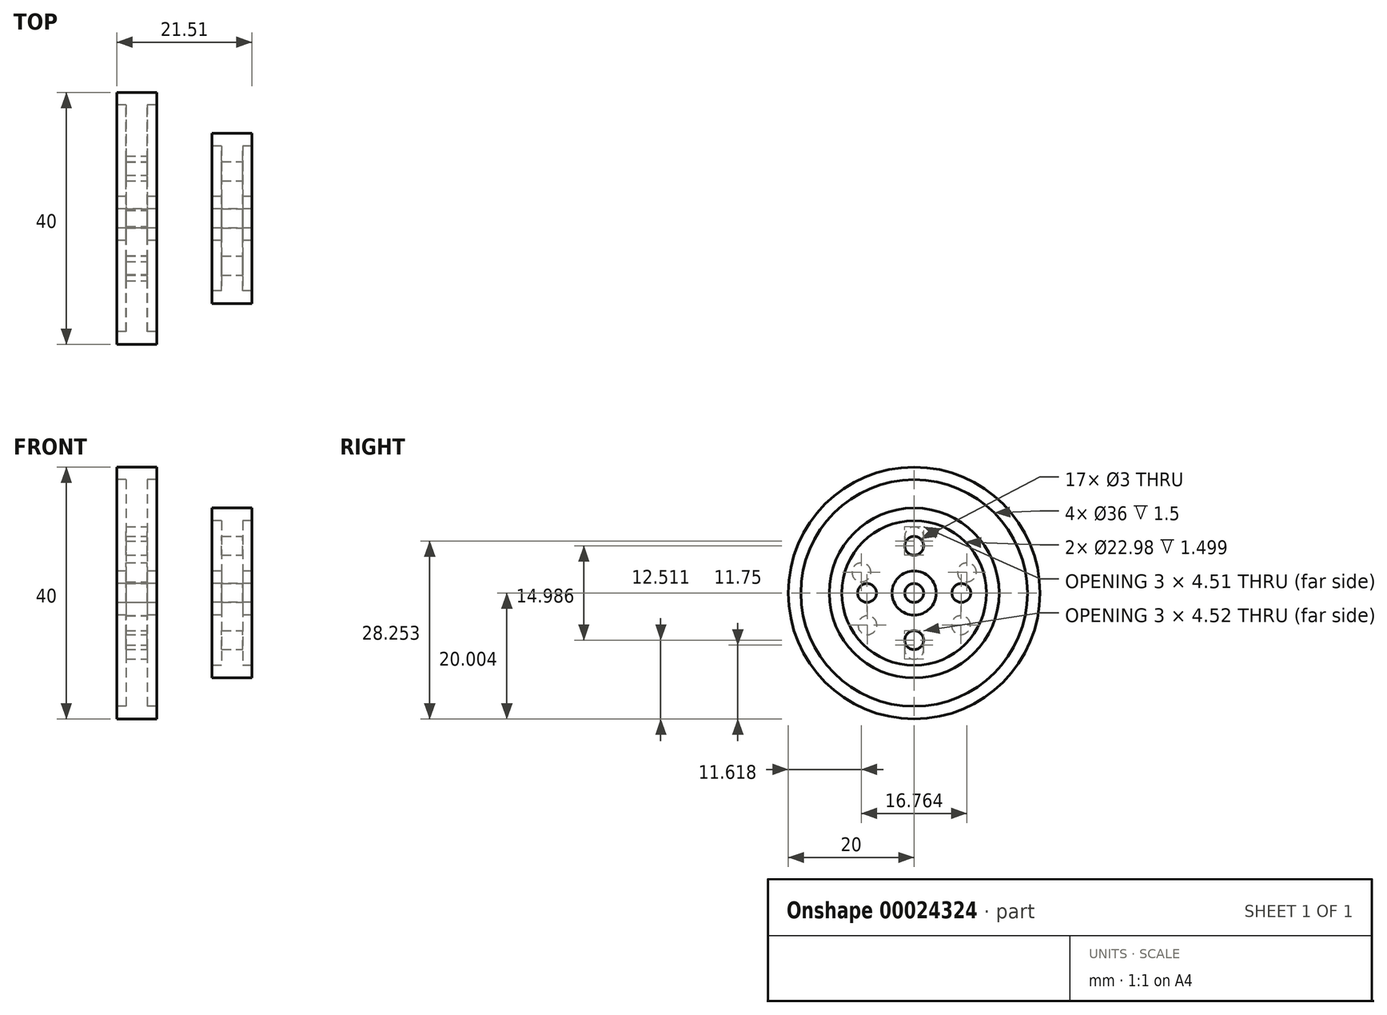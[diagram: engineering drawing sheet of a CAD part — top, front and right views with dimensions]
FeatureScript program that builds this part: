
annotation { "Feature Type Name" : "Feature", "Feature Type Description" : "" }
export const myFeature = defineFeature(function(context is Context, id is Id, definition is map)
    precondition{}
    {
        {
            var Q0;
            Q0=qCreatedBy(makeId("Front.planeOp"),FACE);
            var sketch = newSketch(context, id + "F0", { "sketchPlane" : qUnion([Q0])});
            skLineSegment(sketch, "E0.bottom", {"start": v(-7.32, 15.41) * mm, "end": v(-3.97, 15.41) * mm});
            skLineSegment(sketch, "E0.top", {"start": v(-7.32, -3.09) * mm, "end": v(-3.97, -3.09) * mm});
            skLineSegment(sketch, "E0.left", {"start": v(-7.32, 15.41) * mm, "end": v(-7.32, -3.09) * mm});
            skLineSegment(sketch, "E0.right", {"start": v(-3.97, 15.41) * mm, "end": v(-3.97, -3.09) * mm});
            skLineSegment(sketch, "E1.bottom", {"start": v(-8.82, -3.09) * mm, "end": v(-2.47, -3.09) * mm});
            skLineSegment(sketch, "E1.top", {"start": v(-8.82, -1.09) * mm, "end": v(-2.47, -1.09) * mm});
            skLineSegment(sketch, "E1.left", {"start": v(-8.82, -3.09) * mm, "end": v(-8.82, -1.09) * mm});
            skLineSegment(sketch, "E1.right", {"start": v(-2.47, -3.09) * mm, "end": v(-2.47, -1.09) * mm});
            skLineSegment(sketch, "E2.bottom", {"start": v(-8.82, 15.41) * mm, "end": v(-2.47, 15.41) * mm});
            skLineSegment(sketch, "E2.top", {"start": v(-8.82, 13.41) * mm, "end": v(-2.47, 13.41) * mm});
            skLineSegment(sketch, "E2.left", {"start": v(-8.82, 15.41) * mm, "end": v(-8.82, 13.41) * mm});
            skLineSegment(sketch, "E2.right", {"start": v(-2.47, 15.41) * mm, "end": v(-2.47, 13.41) * mm});
            skLineSegment(sketch, "E3", {"start": v(-32.48, -4.59) * mm, "end": v(21.8, -4.59) * mm, "construction": true});
            skLineSegment(sketch, "E4.bottom", {"start": v(7.84, 7.79) * mm, "end": v(11.2, 7.79) * mm});
            skLineSegment(sketch, "E4.top", {"start": v(7.84, -2.08) * mm, "end": v(11.2, -2.08) * mm});
            skLineSegment(sketch, "E4.left", {"start": v(7.84, 7.79) * mm, "end": v(7.84, -2.08) * mm});
            skLineSegment(sketch, "E4.right", {"start": v(11.2, 7.79) * mm, "end": v(11.2, -2.08) * mm});
            skLineSegment(sketch, "E5.bottom", {"start": v(6.34, -1.08) * mm, "end": v(12.7, -1.08) * mm});
            skLineSegment(sketch, "E5.top", {"start": v(6.34, -3.09) * mm, "end": v(12.7, -3.09) * mm});
            skLineSegment(sketch, "E5.left", {"start": v(6.34, -1.08) * mm, "end": v(6.34, -3.09) * mm});
            skLineSegment(sketch, "E5.right", {"start": v(12.7, -1.08) * mm, "end": v(12.7, -3.09) * mm});
            skLineSegment(sketch, "E6.bottom", {"start": v(6.34, 8.91) * mm, "end": v(12.7, 8.91) * mm});
            skLineSegment(sketch, "E6.top", {"start": v(6.34, 6.9) * mm, "end": v(12.7, 6.9) * mm});
            skLineSegment(sketch, "E6.left", {"start": v(6.34, 8.91) * mm, "end": v(6.34, 6.9) * mm});
            skLineSegment(sketch, "E6.right", {"start": v(12.7, 8.91) * mm, "end": v(12.7, 6.9) * mm});
            skSolve(sketch);
        }
        {
            var Q0;
            {var subQ0=sQuery(id+"F0.wireOp",EDGE,"E2.left");Q0=makeQuery(id+"F0.imprint","IMPRINT",FACE,{"disambiguationData":[TD([[makeQuery(id+"F0.imprint","IMPRINT",EDGE,{"derivedFrom":subQ0}),1.0]])]});}
            var Q1;
            {var subQ3=sQuery(id+"F0.wireOp",EDGE,"E0.left");var subQ5=sQuery(id+"F0.wireOp",EDGE,"E2.bottom");var subQ7=makeQuery(id+"F0.imprint","INTERSECT",VERTEX,{"derivedFrom":[subQ3,subQ5]});Q1=makeQuery(id+"F0.imprint","IMPRINT",FACE,{"disambiguationData":[TD([[makeQuery(id+"F0.imprint","IMPRINT",EDGE,{"disambiguationData":[TD([[subQ7,-1.0]])],"derivedFrom":subQ3}),1.0]])]});}
            var Q2;
            {var subQ0=sQuery(id+"F0.wireOp",EDGE,"E2.right");Q2=makeQuery(id+"F0.imprint","IMPRINT",FACE,{"disambiguationData":[TD([[makeQuery(id+"F0.imprint","IMPRINT",EDGE,{"derivedFrom":subQ0}),-1.0]])]});}
            var Q3;
            {var subQ0=sQuery(id+"F0.wireOp",EDGE,"E2.top");var subQ3=sQuery(id+"F0.wireOp",EDGE,"E0.left");var subQ4=makeQuery(id+"F0.imprint","INTERSECT",VERTEX,{"derivedFrom":[subQ3,subQ0]});Q3=makeQuery(id+"F0.imprint","IMPRINT",FACE,{"disambiguationData":[TD([[makeQuery(id+"F0.imprint","IMPRINT",EDGE,{"disambiguationData":[TD([[subQ4,-1.0]])],"derivedFrom":subQ3}),1.0]])]});}
            var Q4;
            {var subQ0=sQuery(id+"F0.wireOp",EDGE,"E1.left");Q4=makeQuery(id+"F0.imprint","IMPRINT",FACE,{"disambiguationData":[TD([[makeQuery(id+"F0.imprint","IMPRINT",EDGE,{"derivedFrom":subQ0}),-1.0]])]});}
            var Q5;
            {var subQ3=sQuery(id+"F0.wireOp",EDGE,"E0.left");var subQ5=sQuery(id+"F0.wireOp",EDGE,"E1.bottom");var subQ7=makeQuery(id+"F0.imprint","INTERSECT",VERTEX,{"derivedFrom":[subQ3,subQ5]});Q5=makeQuery(id+"F0.imprint","IMPRINT",FACE,{"disambiguationData":[TD([[makeQuery(id+"F0.imprint","IMPRINT",EDGE,{"disambiguationData":[TD([[subQ7,1.0]])],"derivedFrom":subQ3}),1.0]])]});}
            var Q6;
            {var subQ0=sQuery(id+"F0.wireOp",EDGE,"E1.right");Q6=makeQuery(id+"F0.imprint","IMPRINT",FACE,{"disambiguationData":[TD([[makeQuery(id+"F0.imprint","IMPRINT",EDGE,{"derivedFrom":subQ0}),1.0]])]});}
            var Q7;
            Q7=sQuery(id+"F0.wireOp",EDGE,"E3");
            revolve(context, id + "F1", {"entities" : qUnion([Q0, Q1, Q2, Q3, Q4, Q5, Q6]), "axis" : qUnion([Q7]), "revolveType" : RevolveType.FULL});
        }
        {
            var Q0;
            Q0=makeQuery(id+"F1.opRevolve","SWEPT_FACE",FACE,{"disambiguationData":[OSD([sQuery(id+"F0.wireOp",EDGE,"E0.right")])]});
            var sketch = newSketch(context, id + "F2", { "sketchPlane" : qUnion([Q0])});
            skCircle(sketch, "E7", {"center": v(0, 4.42) * mm, "radius": 1.5 * mm});
            skCircle(sketch, "E8", {"center": v(8.38, -1.3) * mm, "radius": 1.5 * mm});
            skCircle(sketch, "E9", {"center": v(7.44, -9.68) * mm, "radius": 1.5 * mm});
            skCircle(sketch, "E10", {"center": v(0, -13.6) * mm, "radius": 1.5 * mm});
            skCircle(sketch, "E11", {"center": v(-7.42, -9.7) * mm, "radius": 1.5 * mm});
            skCircle(sketch, "E12", {"center": v(-8.38, -1.3) * mm, "radius": 1.5 * mm});
            skSolve(sketch);
        }
        {
            var Q0;
            Q0=makeQuery(id+"F2.imprint","IMPRINT",FACE,{"disambiguationData":[TD([[makeQuery(id+"F2.imprint","IMPRINT",EDGE,{"derivedFrom":sQuery(id+"F2.wireOp",EDGE,"E7")}),1.0]])]});
            var Q1;
            Q1=makeQuery(id+"F2.imprint","IMPRINT",FACE,{"disambiguationData":[TD([[makeQuery(id+"F2.imprint","IMPRINT",EDGE,{"derivedFrom":sQuery(id+"F2.wireOp",EDGE,"E8")}),1.0]])]});
            var Q2;
            Q2=makeQuery(id+"F2.imprint","IMPRINT",FACE,{"disambiguationData":[TD([[makeQuery(id+"F2.imprint","IMPRINT",EDGE,{"derivedFrom":sQuery(id+"F2.wireOp",EDGE,"E9")}),1.0]])]});
            var Q3;
            Q3=makeQuery(id+"F2.imprint","IMPRINT",FACE,{"disambiguationData":[TD([[makeQuery(id+"F2.imprint","IMPRINT",EDGE,{"derivedFrom":sQuery(id+"F2.wireOp",EDGE,"E10")}),1.0]])]});
            var Q4;
            Q4=makeQuery(id+"F2.imprint","IMPRINT",FACE,{"disambiguationData":[TD([[makeQuery(id+"F2.imprint","IMPRINT",EDGE,{"derivedFrom":sQuery(id+"F2.wireOp",EDGE,"E11")}),1.0]])]});
            var Q5;
            Q5=makeQuery(id+"F2.imprint","IMPRINT",FACE,{"disambiguationData":[TD([[makeQuery(id+"F2.imprint","IMPRINT",EDGE,{"derivedFrom":sQuery(id+"F2.wireOp",EDGE,"E12")}),1.0]])]});
            extrude(context, id + "F3", {"entities" : qUnion([Q0, Q1, Q2, Q3, Q4, Q5]), "operationType" : NewBodyOperationType.REMOVE, "endBound" : BoundingType.THROUGH_ALL, "oppositeDirection" : true, "depth" : 25.4 * mm});
        }
        {
            var Q0;
            {var subQ0=sQuery(id+"F0.wireOp",EDGE,"E2.left");Q0=makeQuery(id+"F0.imprint","IMPRINT",FACE,{"disambiguationData":[TD([[makeQuery(id+"F0.imprint","IMPRINT",EDGE,{"derivedFrom":subQ0}),1.0]])]});}
            var Q1;
            {var subQ0=sQuery(id+"F0.wireOp",EDGE,"E1.left");Q1=makeQuery(id+"F0.imprint","IMPRINT",FACE,{"disambiguationData":[TD([[makeQuery(id+"F0.imprint","IMPRINT",EDGE,{"derivedFrom":subQ0}),-1.0]])]});}
            var Q2;
            {var subQ0=sQuery(id+"F0.wireOp",EDGE,"E2.right");Q2=makeQuery(id+"F0.imprint","IMPRINT",FACE,{"disambiguationData":[TD([[makeQuery(id+"F0.imprint","IMPRINT",EDGE,{"derivedFrom":subQ0}),-1.0]])]});}
            var Q3;
            {var subQ0=sQuery(id+"F0.wireOp",EDGE,"E1.right");Q3=makeQuery(id+"F0.imprint","IMPRINT",FACE,{"disambiguationData":[TD([[makeQuery(id+"F0.imprint","IMPRINT",EDGE,{"derivedFrom":subQ0}),1.0]])]});}
            var Q4;
            {var subQ7=sQuery(id+"F0.wireOp",EDGE,"E4.top");Q4=makeQuery(id+"F0.imprint","IMPRINT",FACE,{"disambiguationData":[TD([[makeQuery(id+"F0.imprint","IMPRINT",EDGE,{"derivedFrom":subQ7}),-1.0]])]});}
            var Q5;
            {var subQ0=sQuery(id+"F0.wireOp",EDGE,"E2.top");var subQ3=sQuery(id+"F0.wireOp",EDGE,"E0.left");var subQ4=makeQuery(id+"F0.imprint","INTERSECT",VERTEX,{"derivedFrom":[subQ3,subQ0]});Q5=makeQuery(id+"F0.imprint","IMPRINT",FACE,{"disambiguationData":[TD([[makeQuery(id+"F0.imprint","IMPRINT",EDGE,{"disambiguationData":[TD([[subQ4,-1.0]])],"derivedFrom":subQ3}),1.0]])]});}
            var Q6;
            {var subQ5=sQuery(id+"F0.wireOp",EDGE,"E4.bottom");Q6=makeQuery(id+"F0.imprint","IMPRINT",FACE,{"disambiguationData":[TD([[makeQuery(id+"F0.imprint","IMPRINT",EDGE,{"derivedFrom":subQ5}),-1.0]])]});}
            var Q7;
            {var subQ3=sQuery(id+"F0.wireOp",EDGE,"E4.top");Q7=makeQuery(id+"F0.imprint","IMPRINT",FACE,{"disambiguationData":[TD([[makeQuery(id+"F0.imprint","IMPRINT",EDGE,{"derivedFrom":subQ3}),1.0]])]});}
            var Q8;
            {var subQ3=sQuery(id+"F0.wireOp",EDGE,"E0.left");var subQ5=sQuery(id+"F0.wireOp",EDGE,"E2.bottom");var subQ7=makeQuery(id+"F0.imprint","INTERSECT",VERTEX,{"derivedFrom":[subQ3,subQ5]});Q8=makeQuery(id+"F0.imprint","IMPRINT",FACE,{"disambiguationData":[TD([[makeQuery(id+"F0.imprint","IMPRINT",EDGE,{"disambiguationData":[TD([[subQ7,-1.0]])],"derivedFrom":subQ3}),1.0]])]});}
            var Q9;
            {var subQ3=sQuery(id+"F0.wireOp",EDGE,"E0.left");var subQ5=sQuery(id+"F0.wireOp",EDGE,"E1.bottom");var subQ7=makeQuery(id+"F0.imprint","INTERSECT",VERTEX,{"derivedFrom":[subQ3,subQ5]});Q9=makeQuery(id+"F0.imprint","IMPRINT",FACE,{"disambiguationData":[TD([[makeQuery(id+"F0.imprint","IMPRINT",EDGE,{"disambiguationData":[TD([[subQ7,1.0]])],"derivedFrom":subQ3}),1.0]])]});}
            var Q10;
            {var subQ0=sQuery(id+"F0.wireOp",EDGE,"E6.top");var subQ3=sQuery(id+"F0.wireOp",EDGE,"E4.left");var subQ4=makeQuery(id+"F0.imprint","INTERSECT",VERTEX,{"derivedFrom":[subQ3,subQ0]});Q10=makeQuery(id+"F0.imprint","IMPRINT",FACE,{"disambiguationData":[TD([[makeQuery(id+"F0.imprint","IMPRINT",EDGE,{"disambiguationData":[TD([[subQ4,-1.0]])],"derivedFrom":subQ3}),1.0]])]});}
            var Q11;
            {var subQ7=sQuery(id+"F0.wireOp",EDGE,"E4.bottom");Q11=makeQuery(id+"F0.imprint","IMPRINT",FACE,{"disambiguationData":[TD([[makeQuery(id+"F0.imprint","IMPRINT",EDGE,{"derivedFrom":subQ7}),1.0]])]});}
            var Q12;
            Q12=sQuery(id+"F0.wireOp",EDGE,"E3");
            revolve(context, id + "F4", {"entities" : qUnion([Q0, Q1, Q2, Q3, Q4, Q5, Q6, Q7, Q8, Q9, Q10, Q11]), "axis" : qUnion([Q12]), "revolveType" : RevolveType.FULL});
        }
        {
            var Q0;
            Q0=makeQuery(id+"F4.opRevolve","SWEPT_FACE",FACE,{"disambiguationData":[OSD([sQuery(id+"F0.wireOp",EDGE,"E4.right")])]});
            var sketch = newSketch(context, id + "F5", { "sketchPlane" : qUnion([Q0])});
            skCircle(sketch, "E13", {"center": v(0, 2.9) * mm, "radius": 1.5 * mm});
            skCircle(sketch, "E14", {"center": v(7.5, -4.58) * mm, "radius": 1.5 * mm});
            skCircle(sketch, "E15", {"center": v(0, -12.08) * mm, "radius": 1.5 * mm});
            skCircle(sketch, "E16", {"center": v(-7.5, -4.58) * mm, "radius": 1.5 * mm});
            skLineSegment(sketch, "E17", {"start": v(0, 6.9) * mm, "end": v(0, -1.08) * mm, "construction": true});
            skSolve(sketch);
        }
        {
            var Q0;
            Q0=makeQuery(id+"F5.imprint","IMPRINT",FACE,{"disambiguationData":[TD([[makeQuery(id+"F5.imprint","IMPRINT",EDGE,{"derivedFrom":sQuery(id+"F5.wireOp",EDGE,"E13")}),1.0]])]});
            var Q1;
            Q1=makeQuery(id+"F5.imprint","IMPRINT",FACE,{"disambiguationData":[TD([[makeQuery(id+"F5.imprint","IMPRINT",EDGE,{"derivedFrom":sQuery(id+"F5.wireOp",EDGE,"E14")}),1.0]])]});
            var Q2;
            Q2=makeQuery(id+"F5.imprint","IMPRINT",FACE,{"disambiguationData":[TD([[makeQuery(id+"F5.imprint","IMPRINT",EDGE,{"derivedFrom":sQuery(id+"F5.wireOp",EDGE,"E15")}),1.0]])]});
            var Q3;
            Q3=makeQuery(id+"F5.imprint","IMPRINT",FACE,{"disambiguationData":[TD([[makeQuery(id+"F5.imprint","IMPRINT",EDGE,{"derivedFrom":sQuery(id+"F5.wireOp",EDGE,"E16")}),1.0]])]});
            extrude(context, id + "F6", {"entities" : qUnion([Q0, Q1, Q2, Q3]), "operationType" : NewBodyOperationType.REMOVE, "endBound" : BoundingType.THROUGH_ALL, "oppositeDirection" : true, "depth" : 25.4 * mm});
        }
    });
